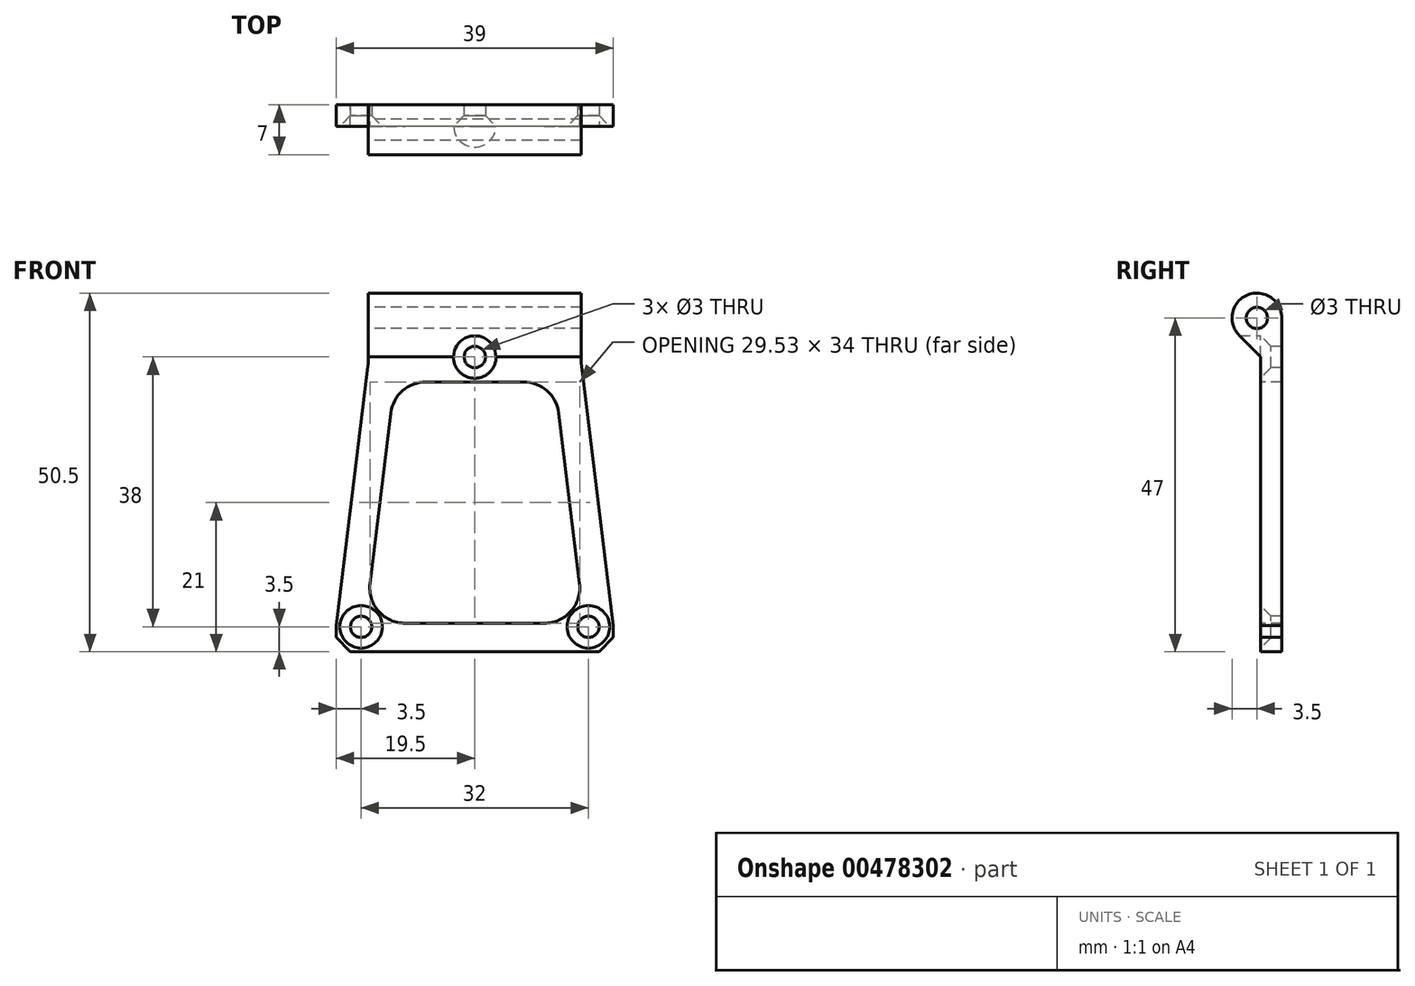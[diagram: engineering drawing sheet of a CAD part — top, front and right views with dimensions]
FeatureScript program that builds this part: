
annotation { "Feature Type Name" : "Feature", "Feature Type Description" : "" }
export const myFeature = defineFeature(function(context is Context, id is Id, definition is map)
    precondition{}
    {
        {
            var Q0;
            Q0=qCreatedBy(makeId("Front.planeOp"),FACE);
            var sketch = newSketch(context, id + "F0", { "sketchPlane" : qUnion([Q0])});
            skLineSegment(sketch, "E0", {"start": v(0, 19) * mm, "end": v(0, -19) * mm, "construction": true});
            skPoint(sketch, "E1", {"position": v(0, 0) * mm});
            skPoint(sketch, "E2.MirrorP", {"position": v(16, -19) * mm});
            skLineSegment(sketch, "E3", {"start": v(0, -22.5) * mm, "end": v(19.5, -22.5) * mm});
            skLineSegment(sketch, "E4", {"start": v(19.5, -22.5) * mm, "end": v(19.5, -18.79) * mm});
            skLineSegment(sketch, "E5", {"start": v(19.5, -18.79) * mm, "end": v(15, 18) * mm});
            skLineSegment(sketch, "E6", {"start": v(15, 18) * mm, "end": v(15, 28) * mm});
            skLineSegment(sketch, "E7", {"start": v(15, 28) * mm, "end": v(0, 28) * mm});
            skCircle(sketch, "E8", {"center": v(16, -19) * mm, "radius": 3.5 * mm, "construction": true});
            skLineSegment(sketch, "E9", {"start": v(0, 15.5) * mm, "end": v(11.28, 15.5) * mm});
            skLineSegment(sketch, "E10", {"start": v(11.28, 15.5) * mm, "end": v(15.44, -18.5) * mm});
            skLineSegment(sketch, "E11", {"start": v(15.44, -18.5) * mm, "end": v(0, -18.5) * mm});
            skLineSegment(sketch, "E12.MirrorCS", {"start": v(0, 15.5) * mm, "end": v(-11.28, 15.5) * mm});
            skLineSegment(sketch, "E13.MirrorCS", {"start": v(-15, 28) * mm, "end": v(0, 28) * mm});
            skLineSegment(sketch, "E14.MirrorCS", {"start": v(-15, 18) * mm, "end": v(-15, 28) * mm});
            skLineSegment(sketch, "E15.MirrorCS", {"start": v(-19.5, -18.79) * mm, "end": v(-15, 18) * mm});
            skLineSegment(sketch, "E16.MirrorCS", {"start": v(-11.28, 15.5) * mm, "end": v(-15.44, -18.5) * mm});
            skLineSegment(sketch, "E17.MirrorCS", {"start": v(-19.5, -22.5) * mm, "end": v(-19.5, -18.79) * mm});
            skLineSegment(sketch, "E18.MirrorCS", {"start": v(0, -22.5) * mm, "end": v(-19.5, -22.5) * mm});
            skLineSegment(sketch, "E19.MirrorCS", {"start": v(-15.44, -18.5) * mm, "end": v(0, -18.5) * mm});
            skCircle(sketch, "E20.MirrorC", {"center": v(-16, -19) * mm, "radius": 3.5 * mm, "construction": true});
            skSolve(sketch);
        }
        {
            var Q0;
            Q0=makeQuery(id+"F0.imprint","IMPRINT",FACE,{"disambiguationData":[TD([[makeQuery(id+"F0.imprint","IMPRINT",EDGE,{"derivedFrom":sQuery(id+"F0.wireOp",EDGE,"E3")}),1.0]])]});
            var Q1;
            Q1=makeQuery(id+"F0.imprint","IMPRINT",FACE,{"disambiguationData":[TD([[makeQuery(id+"F0.imprint","IMPRINT",EDGE,{"derivedFrom":sQuery(id+"F0.wireOp",EDGE,"E9")}),1.0]])]});
            var Q2;
            {var subQ3=sQuery(id+"F0.wireOp",EDGE,"E6");Q2=makeQuery(id+"F0.imprint","IMPRINT",FACE,{"disambiguationData":[TD([[makeQuery(id+"F0.imprint","IMPRINT",EDGE,{"derivedFrom":subQ3}),1.0]])]});}
            extrude(context, id + "F1", {"entities" : qUnion([Q0, Q1, Q2]), "oppositeDirection" : true, "depth" : 3 * mm, "offsetDistance" : 25 * mm});
        }
        {
            var Q0;
            Q0=makeQuery(id+"F1.opExtrude","SWEPT_EDGE",EDGE,{"disambiguationData":[OSD([sQuery(id+"F0.wireOp",EDGE,"E14.MirrorCS"),sQuery(id+"F0.wireOp",EDGE,"E15.MirrorCS")])]});
            var Q1;
            Q1=makeQuery(id+"F1.opExtrude","SWEPT_EDGE",EDGE,{"disambiguationData":[OSD([sQuery(id+"F0.wireOp",EDGE,"E12.MirrorCS"),sQuery(id+"F0.wireOp",EDGE,"E16.MirrorCS")])]});
            var Q2;
            Q2=makeQuery(id+"F1.opExtrude","SWEPT_EDGE",EDGE,{"disambiguationData":[OSD([sQuery(id+"F0.wireOp",EDGE,"E9"),sQuery(id+"F0.wireOp",EDGE,"E10")])]});
            var Q3;
            Q3=makeQuery(id+"F1.opExtrude","SWEPT_EDGE",EDGE,{"disambiguationData":[OSD([sQuery(id+"F0.wireOp",EDGE,"E10"),sQuery(id+"F0.wireOp",EDGE,"E11")])]});
            var Q4;
            Q4=makeQuery(id+"F1.opExtrude","SWEPT_EDGE",EDGE,{"disambiguationData":[OSD([sQuery(id+"F0.wireOp",EDGE,"E16.MirrorCS"),sQuery(id+"F0.wireOp",EDGE,"E19.MirrorCS")])]});
            var Q5;
            Q5=makeQuery(id+"F1.opExtrude","SWEPT_EDGE",EDGE,{"disambiguationData":[OSD([sQuery(id+"F0.wireOp",EDGE,"E5"),sQuery(id+"F0.wireOp",EDGE,"E6")])]});
            fillet(context, id + "F2", {"entities" : qUnion([Q0, Q1, Q2, Q3, Q4, Q5]), "radius" : 5 * mm, "tangentPropagation" : true, "allowEdgeOverflow" : false});
        }
        {
            var Q0;
            Q0=makeQuery(id+"F1.opExtrude","SWEPT_EDGE",EDGE,{"disambiguationData":[OSD([sQuery(id+"F0.wireOp",EDGE,"E17.MirrorCS"),sQuery(id+"F0.wireOp",EDGE,"E18.MirrorCS")])]});
            var Q1;
            Q1=makeQuery(id+"F1.opExtrude","SWEPT_EDGE",EDGE,{"disambiguationData":[OSD([sQuery(id+"F0.wireOp",EDGE,"E3"),sQuery(id+"F0.wireOp",EDGE,"E4")])]});
            chamfer(context, id + "F3", {"entities" : qUnion([Q0, Q1]), "width" : 2 * mm, "tangentPropagation" : true});
        }
        {
            var Q0;
            Q0=makeQuery(id+"F1.opExtrude","SWEPT_FACE",FACE,{"disambiguationData":[OSD([sQuery(id+"F0.wireOp",EDGE,"E14.MirrorCS")])]});
            var sketch = newSketch(context, id + "F4", { "sketchPlane" : qUnion([Q0])});
            skCircle(sketch, "E21", {"center": v(0.5, 24.5) * mm, "radius": 1.5 * mm});
            skCircle(sketch, "E22.0", {"center": v(0.5, 24.5) * mm, "radius": 3.5 * mm});
            skLineSegment(sketch, "E23", {"start": v(2.97, 22.03) * mm, "end": v(0, 19.05) * mm});
            skSolve(sketch);
        }
        {
            var Q0;
            {var subQ1=sQuery(id+"F0.wireOp",EDGE,"E14.MirrorCS");var subQ6=makeQuery(id+"F1.opExtrude","SWEPT_EDGE",EDGE,{"disambiguationData":[OSD([sQuery(id+"F0.wireOp",EDGE,"E13.MirrorCS"),subQ1])]});Q0=makeQuery(id+"F4.imprint","IMPRINT",FACE,{"disambiguationData":[TD([[makeQuery(id+"F4.imprint","IMPRINT",EDGE,{"derivedFrom":subQ6}),-1.0]])]});}
            var Q1;
            {var subQ0=sQuery(id+"F4.wireOp",EDGE,"E21");var subQ1=makeQuery(id+"F1.opExtrude","CAP_EDGE",EDGE,{"disambiguationData":[OSD([sQuery(id+"F0.wireOp",EDGE,"E14.MirrorCS")])],"isStart":true});var subQ2=makeQuery(id+"F4.imprint","INTERSECT",VERTEX,{"disambiguationData":[OD(0.0)],"derivedFrom":[subQ1,subQ0]});Q1=makeQuery(id+"F4.imprint","IMPRINT",FACE,{"disambiguationData":[TD([[makeQuery(id+"F4.imprint","IMPRINT",EDGE,{"disambiguationData":[TD([[subQ2,1.0]])],"derivedFrom":subQ0}),1.0]])]});}
            var Q2;
            {var subQ0=sQuery(id+"F4.wireOp",EDGE,"E21");var subQ1=makeQuery(id+"FKyR0qUEHPLwvTp_1.opExtrude","CAP_EDGE",EDGE,{"disambiguationData":[OSD([sQuery(id+"F0.wireOp",EDGE,"E14.MirrorCS")])],"isStart":false});var subQ2=makeQuery(id+"F4.imprint","INTERSECT",VERTEX,{"disambiguationData":[OD(0.0)],"derivedFrom":[subQ1,subQ0]});Q2=makeQuery(id+"F4.imprint","IMPRINT",FACE,{"disambiguationData":[TD([[makeQuery(id+"F4.imprint","IMPRINT",EDGE,{"disambiguationData":[TD([[subQ2,-1.0]])],"derivedFrom":subQ0}),1.0]])]});}
            extrude(context, id + "F5", {"entities" : qUnion([Q0, Q1, Q2]), "operationType" : NewBodyOperationType.REMOVE, "endBound" : BoundingType.THROUGH_ALL, "oppositeDirection" : true, "depth" : 25 * mm, "offsetDistance" : 25 * mm});
        }
        {
            var Q0;
            {var subQ2=makeQuery(id+"F1.opExtrude","CAP_EDGE",EDGE,{"disambiguationData":[OSD([sQuery(id+"F0.wireOp",EDGE,"E14.MirrorCS")])],"isStart":true});var subQ4=sQuery(id+"F4.wireOp",EDGE,"E21");var subQ5=makeQuery(id+"F4.imprint","INTERSECT",VERTEX,{"disambiguationData":[OD(0.0)],"derivedFrom":[subQ2,subQ4]});Q0=makeQuery(id+"F4.imprint","IMPRINT",FACE,{"disambiguationData":[TD([[makeQuery(id+"F4.imprint","IMPRINT",EDGE,{"disambiguationData":[TD([[subQ5,1.0]])],"derivedFrom":subQ4}),-1.0]])]});}
            var Q1;
            {var subQ0=sQuery(id+"F4.wireOp",EDGE,"E23");Q1=makeQuery(id+"F4.imprint","IMPRINT",FACE,{"disambiguationData":[TD([[makeQuery(id+"F4.imprint","IMPRINT",EDGE,{"derivedFrom":subQ0}),-1.0]])]});}
            var Q2;
            Q2=makeQuery(id+"F1.opExtrude","SWEPT_FACE",FACE,{"disambiguationData":[OSD([sQuery(id+"F0.wireOp",EDGE,"E6")])]});
            extrude(context, id + "F6", {"entities" : qUnion([Q0, Q1]), "operationType" : NewBodyOperationType.ADD, "endBound" : BoundingType.UP_TO_SURFACE, "oppositeDirection" : true, "depth" : 25 * mm, "endBoundEntityFace" : qUnion([Q2]), "offsetDistance" : 25 * mm});
        }
        {
            var Q0;
            Q0=sQuery(id+"F0.wireOp",VERTEX,"E0.start");
            var Q1;
            Q1=makeQuery(id+"F1.opExtrude","SWEPT_BODY",BODY,{"disambiguationData":[OSD([sQuery(id+"F0.wireOp",EDGE,"E3"),sQuery(id+"F0.wireOp",EDGE,"E4"),sQuery(id+"F0.wireOp",EDGE,"E5"),sQuery(id+"F0.wireOp",EDGE,"E6"),sQuery(id+"F0.wireOp",EDGE,"E7"),sQuery(id+"F0.wireOp",EDGE,"E9"),sQuery(id+"F0.wireOp",EDGE,"E10"),sQuery(id+"F0.wireOp",EDGE,"E11"),sQuery(id+"F0.wireOp",EDGE,"E12.MirrorCS"),sQuery(id+"F0.wireOp",EDGE,"E13.MirrorCS"),sQuery(id+"F0.wireOp",EDGE,"E14.MirrorCS"),sQuery(id+"F0.wireOp",EDGE,"E15.MirrorCS"),sQuery(id+"F0.wireOp",EDGE,"E16.MirrorCS"),sQuery(id+"F0.wireOp",EDGE,"E17.MirrorCS"),sQuery(id+"F0.wireOp",EDGE,"E18.MirrorCS"),sQuery(id+"F0.wireOp",EDGE,"E19.MirrorCS")])]});
            hole(context, id + "F7", {"style" : HoleStyle.SIMPLE, "endStyle" : HoleEndStyle.THROUGH, "oppositeDirection" : true, "holeDiameter" : 6 * mm, "isTappedThrough" : true, "tappedDepth" : 12 * mm, "tapClearance" : 3, "startFromSketch" : true, "locations" : qUnion([Q0]), "scope" : qUnion([Q1])});
        }
        {
            var Q0;
            Q0=sQuery(id+"F0.wireOp",VERTEX,"E0.start");
            var Q1;
            Q1=sQuery(id+"F0.wireOp",VERTEX,"E20.MirrorC.center");
            var Q2;
            Q2=sQuery(id+"F0.wireOp",VERTEX,"E2.MirrorP");
            var Q3;
            Q3=makeQuery(id+"F1.opExtrude","SWEPT_BODY",BODY,{"disambiguationData":[OSD([sQuery(id+"F0.wireOp",EDGE,"E3"),sQuery(id+"F0.wireOp",EDGE,"E4"),sQuery(id+"F0.wireOp",EDGE,"E5"),sQuery(id+"F0.wireOp",EDGE,"E6"),sQuery(id+"F0.wireOp",EDGE,"E7"),sQuery(id+"F0.wireOp",EDGE,"E9"),sQuery(id+"F0.wireOp",EDGE,"E10"),sQuery(id+"F0.wireOp",EDGE,"E11"),sQuery(id+"F0.wireOp",EDGE,"E12.MirrorCS"),sQuery(id+"F0.wireOp",EDGE,"E13.MirrorCS"),sQuery(id+"F0.wireOp",EDGE,"E14.MirrorCS"),sQuery(id+"F0.wireOp",EDGE,"E15.MirrorCS"),sQuery(id+"F0.wireOp",EDGE,"E16.MirrorCS"),sQuery(id+"F0.wireOp",EDGE,"E17.MirrorCS"),sQuery(id+"F0.wireOp",EDGE,"E18.MirrorCS"),sQuery(id+"F0.wireOp",EDGE,"E19.MirrorCS")])]});
            hole(context, id + "F8", {"style" : HoleStyle.C_SINK, "endStyle" : HoleEndStyle.THROUGH, "holeDiameter" : 3 * mm, "cSinkDiameter" : 6 * mm, "cSinkAngle" : 90 * degree, "isTappedThrough" : true, "tappedDepth" : 12 * mm, "tapClearance" : 3, "startFromSketch" : true, "locations" : qUnion([Q0, Q1, Q2]), "scope" : qUnion([Q3])});
        }
    });
